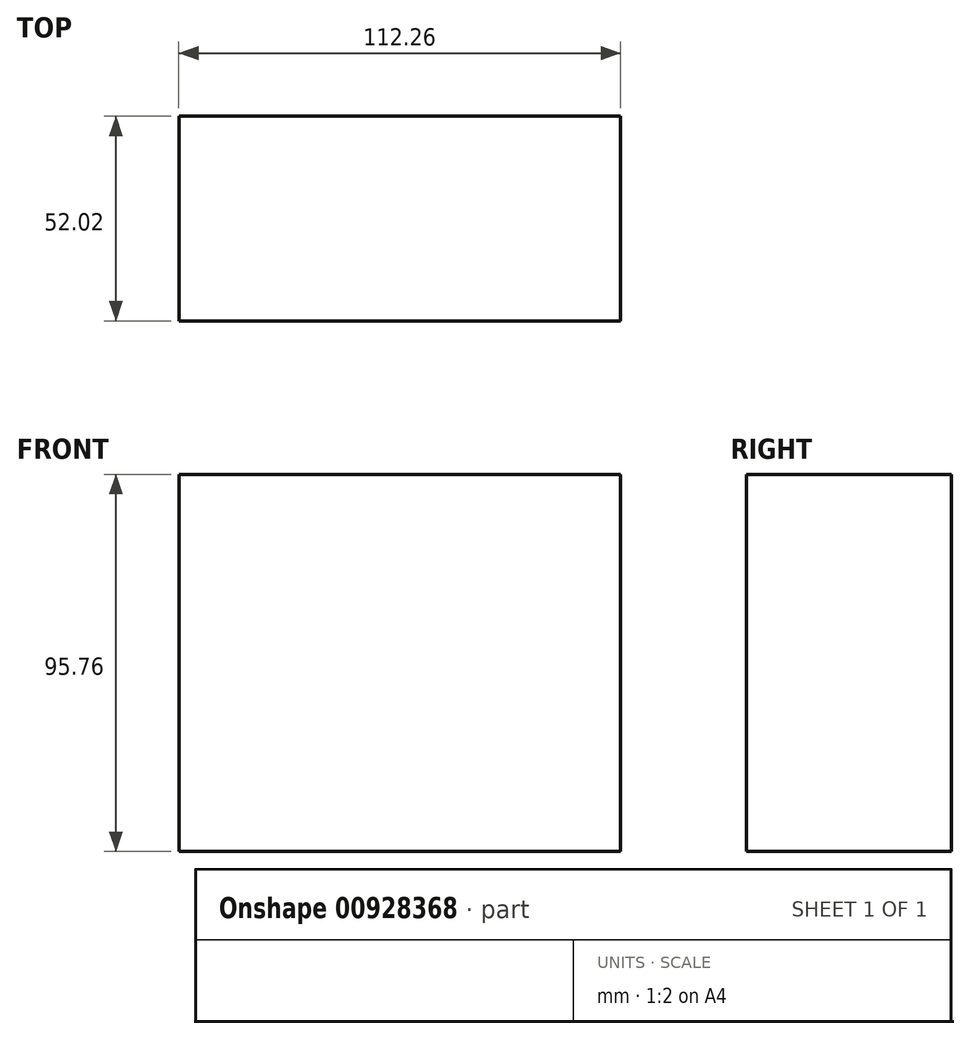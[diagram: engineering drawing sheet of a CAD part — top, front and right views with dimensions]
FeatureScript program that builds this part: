
annotation { "Feature Type Name" : "Feature", "Feature Type Description" : "" }
export const myFeature = defineFeature(function(context is Context, id is Id, definition is map)
    precondition{}
    {
        {
            var Q0;
            Q0=qCreatedBy(makeId("Top.planeOp"),FACE);
            var sketch = newSketch(context, id + "F0", { "sketchPlane" : qUnion([Q0])});
            skLineSegment(sketch, "E0.bottom", {"start": v(-62.78, 0) * mm, "end": v(49.48, 0) * mm});
            skLineSegment(sketch, "E0.top", {"start": v(-62.78, -52.02) * mm, "end": v(49.48, -52.02) * mm});
            skLineSegment(sketch, "E0.left", {"start": v(-62.78, 0) * mm, "end": v(-62.78, -52.02) * mm});
            skLineSegment(sketch, "E0.right", {"start": v(49.48, 0) * mm, "end": v(49.48, -52.02) * mm});
            skSolve(sketch);
        }
        {
            var Q0;
            Q0=makeQuery(id+"F0.imprint","IMPRINT",FACE,{"disambiguationData":[TD([[makeQuery(id+"F0.imprint","IMPRINT",EDGE,{"derivedFrom":sQuery(id+"F0.wireOp",EDGE,"E0.bottom")}),-1.0]])]});
            var sketch = newSketch(context, id + "F1", { "sketchPlane" : qUnion([Q0])});
            skSolve(sketch);
        }
        {
            var Q0;
            Q0=makeQuery(id+"F1.imprint","IMPRINT",FACE,{"disambiguationData":[TD([[makeQuery(id+"F1.imprint","IMPRINT",EDGE,{"derivedFrom":makeQuery(id+"F0.imprint","IMPRINT",EDGE,{"derivedFrom":sQuery(id+"F0.wireOp",EDGE,"E0.bottom")})}),-1.0]])]});
            var Q1;
            Q1=makeQuery(id+"F0.imprint","IMPRINT",FACE,{"disambiguationData":[TD([[makeQuery(id+"F0.imprint","IMPRINT",EDGE,{"derivedFrom":sQuery(id+"F0.wireOp",EDGE,"E0.bottom")}),-1.0]])]});
            extrude(context, id + "F2", {"entities" : qUnion([Q0, Q1]), "depth" : 95.76 * mm, "offsetDistance" : 25.4 * mm});
        }
    });
